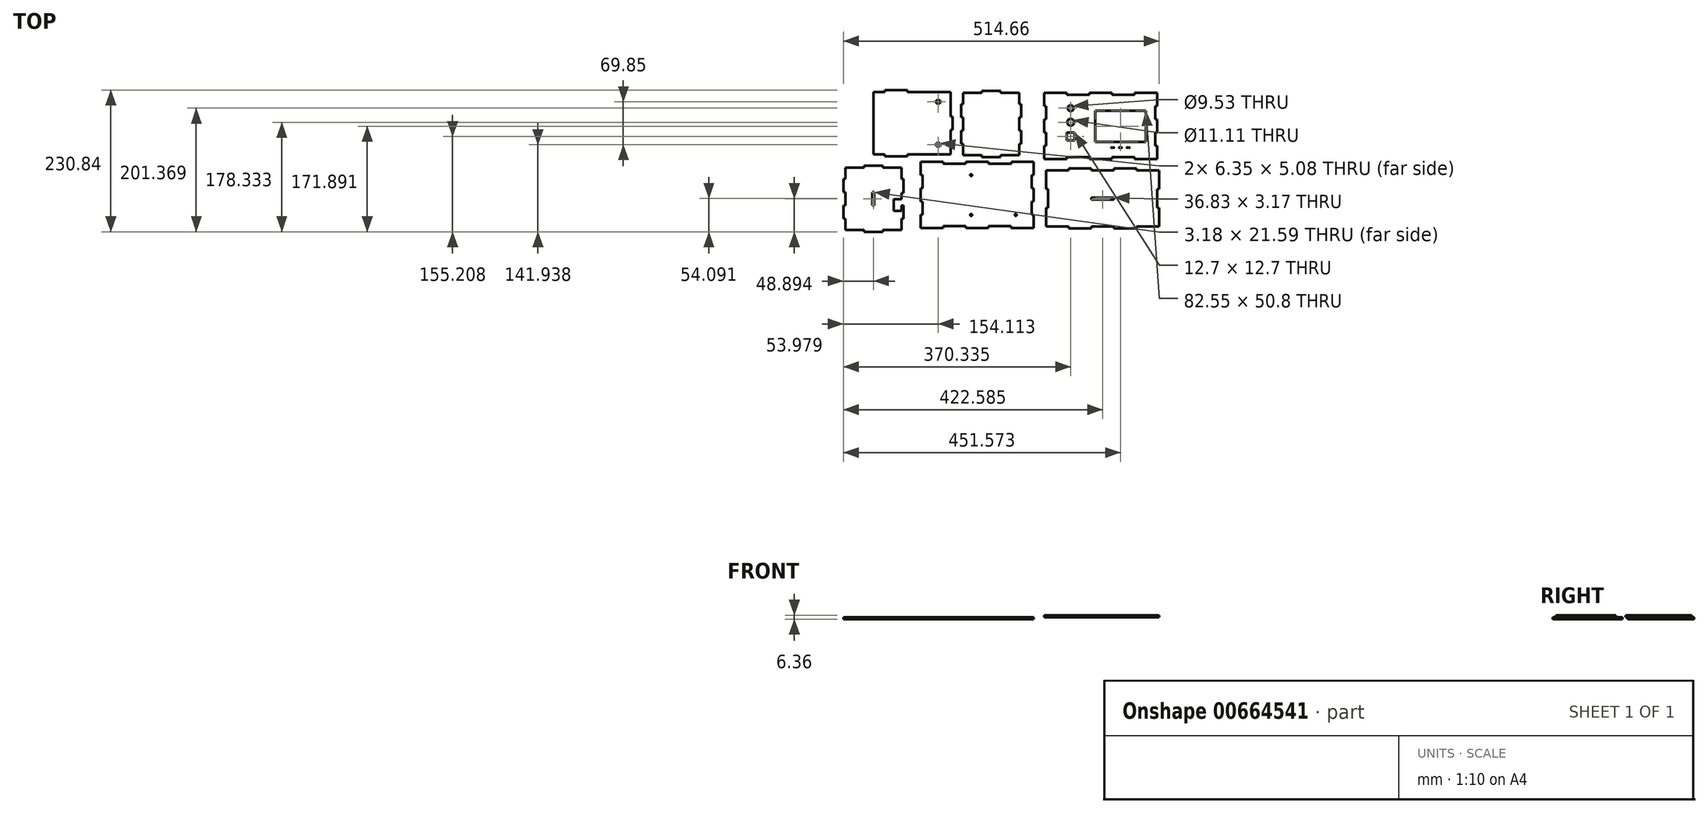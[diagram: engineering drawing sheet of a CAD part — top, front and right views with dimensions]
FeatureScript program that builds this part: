
annotation { "Feature Type Name" : "Feature", "Feature Type Description" : "" }
export const myFeature = defineFeature(function(context is Context, id is Id, definition is map)
    precondition{}
    {
        {
            var Q0;
            Q0=qCreatedBy(makeId("Top.planeOp"),FACE);
            var sketch = newSketch(context, id + "F0", { "sketchPlane" : qUnion([Q0])});
            skLineSegment(sketch, "E0", {"start": v(0, 18.41) * mm, "end": v(0, 40) * mm});
            skLineSegment(sketch, "E1", {"start": v(33.65, 101.6) * mm, "end": v(70.48, 101.6) * mm});
            skLineSegment(sketch, "E2", {"start": v(33.66, 0) * mm, "end": v(70.48, 0) * mm});
            skLineSegment(sketch, "E3", {"start": v(177.8, 18.41) * mm, "end": v(177.8, 40) * mm});
            skCircle(sketch, "E4", {"center": v(39.83, 56.57) * mm, "radius": 5.56 * mm});
            skLineSegment(sketch, "E5.bottom", {"start": v(33.48, 39.8) * mm, "end": v(46.18, 39.8) * mm});
            skLineSegment(sketch, "E5.top", {"start": v(33.48, 27.1) * mm, "end": v(46.18, 27.1) * mm});
            skLineSegment(sketch, "E5.left", {"start": v(33.48, 39.8) * mm, "end": v(33.48, 27.1) * mm});
            skLineSegment(sketch, "E5.right", {"start": v(46.18, 39.8) * mm, "end": v(46.18, 27.1) * mm});
            skPoint(sketch, "E5.middle", {"position": v(39.83, 33.45) * mm});
            skPoint(sketch, "E6.orphan", {"position": v(39.83, 51.02) * mm});
            skPoint(sketch, "E7.trimOffspring.end.orphan", {"position": v(39.83, 15.88) * mm});
            skLineSegment(sketch, "E8", {"start": v(39.83, 56.57) * mm, "end": v(39.83, 62.13) * mm});
            skCircle(sketch, "E9", {"center": v(39.83, 79.6) * mm, "radius": 4.76 * mm});
            skLineSegment(sketch, "E10.bottom", {"start": v(79.79, 75.53) * mm, "end": v(162.34, 75.53) * mm});
            skLineSegment(sketch, "E10.top", {"start": v(79.79, 24.73) * mm, "end": v(162.34, 24.73) * mm});
            skLineSegment(sketch, "E10.left", {"start": v(79.79, 75.53) * mm, "end": v(79.79, 24.73) * mm});
            skLineSegment(sketch, "E10.right", {"start": v(162.34, 75.53) * mm, "end": v(162.34, 24.73) * mm});
            skPoint(sketch, "E10.middle", {"position": v(121.06, 50.13) * mm});
            skPoint(sketch, "E10.middle.positionSnap0", {"position": v(174.63, 50.13) * mm});
            skPoint(sketch, "E10.centerSnap0", {"position": v(174.63, 50.13) * mm});
            skLineSegment(sketch, "E11", {"start": v(122.02, 15.42) * mm, "end": v(122.65, 15.42) * mm});
            skLineSegment(sketch, "E12", {"start": v(122.65, 15.42) * mm, "end": v(123.29, 15.42) * mm});
            skLineSegment(sketch, "E13", {"start": v(132.18, 15.42) * mm, "end": v(132.81, 15.42) * mm});
            skLineSegment(sketch, "E14.MirrorCS", {"start": v(120.11, 15.42) * mm, "end": v(119.48, 15.42) * mm});
            skLineSegment(sketch, "E15.MirrorCS", {"start": v(119.48, 15.42) * mm, "end": v(118.84, 15.42) * mm});
            skLineSegment(sketch, "E16.MirrorCS", {"start": v(109.95, 15.42) * mm, "end": v(109.32, 15.42) * mm});
            skCircle(sketch, "E17", {"center": v(119.48, 15.42) * mm, "radius": 0.64 * mm});
            skCircle(sketch, "E18", {"center": v(122.65, 15.42) * mm, "radius": 0.64 * mm});
            skCircle(sketch, "E19", {"center": v(132.18, 15.42) * mm, "radius": 0.64 * mm});
            skCircle(sketch, "E20", {"center": v(135.35, 15.42) * mm, "radius": 0.64 * mm});
            skCircle(sketch, "E21", {"center": v(109.95, 15.42) * mm, "radius": 0.64 * mm});
            skCircle(sketch, "E22", {"center": v(106.78, 15.42) * mm, "radius": 0.64 * mm});
            skLineSegment(sketch, "E23.trimOffspring", {"start": v(110.59, 15.42) * mm, "end": v(109.95, 15.42) * mm});
            skLineSegment(sketch, "E24.trimOffspring", {"start": v(131.54, 15.42) * mm, "end": v(132.18, 15.42) * mm});
            skLineSegment(sketch, "E25.trimOffspring", {"start": v(134.72, 15.42) * mm, "end": v(135.35, 15.42) * mm});
            skLineSegment(sketch, "E26.trimOffspring", {"start": v(107.41, 15.42) * mm, "end": v(106.78, 15.42) * mm});
            skLineSegment(sketch, "E27.bottom", {"start": v(33.65, 104.77) * mm, "end": v(-3.17, 104.77) * mm});
            skLineSegment(sketch, "E27.left", {"start": v(180.97, 104.78) * mm, "end": v(180.97, 83.19) * mm});
            skPoint(sketch, "E27.middle", {"position": v(88.9, 50.8) * mm});
            skPoint(sketch, "E27.middle.positionSnap0", {"position": v(177.8, 50.8) * mm});
            skPoint(sketch, "E27.middle.positionSnap1", {"position": v(88.9, 101.6) * mm});
            skPoint(sketch, "E27.centerSnap0", {"position": v(177.8, 50.8) * mm});
            skPoint(sketch, "E27.centerSnap1", {"position": v(88.9, 101.6) * mm});
            skLineSegment(sketch, "E28", {"start": v(-3.17, 104.77) * mm, "end": v(33.66, 104.77) * mm});
            skLineSegment(sketch, "E29.bottom", {"start": v(107.31, 104.77) * mm, "end": v(70.48, 104.77) * mm});
            skLineSegment(sketch, "E30.bottom", {"start": v(180.97, 104.78) * mm, "end": v(144.14, 104.78) * mm});
            skLineSegment(sketch, "E31", {"start": v(-3.17, -3.18) * mm, "end": v(33.66, -3.18) * mm});
            skLineSegment(sketch, "E32.bottom", {"start": v(107.31, -3.18) * mm, "end": v(70.48, -3.18) * mm});
            skLineSegment(sketch, "E33.bottom", {"start": v(180.97, -3.18) * mm, "end": v(144.14, -3.18) * mm});
            skLineSegment(sketch, "E34", {"start": v(33.65, 104.77) * mm, "end": v(33.65, 101.6) * mm});
            skLineSegment(sketch, "E35", {"start": v(70.48, 104.77) * mm, "end": v(70.48, 101.6) * mm});
            skLineSegment(sketch, "E36", {"start": v(107.31, 104.77) * mm, "end": v(107.31, 101.6) * mm});
            skLineSegment(sketch, "E37", {"start": v(144.14, 104.77) * mm, "end": v(144.14, 101.6) * mm});
            skLineSegment(sketch, "E38", {"start": v(33.66, -3.18) * mm, "end": v(33.66, 0) * mm});
            skLineSegment(sketch, "E39", {"start": v(70.48, -3.18) * mm, "end": v(70.48, 0) * mm});
            skLineSegment(sketch, "E40", {"start": v(107.31, -3.18) * mm, "end": v(107.31, 0) * mm});
            skLineSegment(sketch, "E41", {"start": v(144.14, -3.18) * mm, "end": v(144.14, 0) * mm});
            skPoint(sketch, "E42.orphan", {"position": v(180.97, -3.17) * mm});
            skLineSegment(sketch, "E43.left", {"start": v(180.97, 18.41) * mm, "end": v(180.97, -3.18) * mm});
            skLineSegment(sketch, "E44.left", {"start": v(180.97, 61.6) * mm, "end": v(180.97, 40) * mm});
            skLineSegment(sketch, "E45", {"start": v(180.97, 83.19) * mm, "end": v(177.8, 83.19) * mm});
            skLineSegment(sketch, "E46", {"start": v(177.8, 83.19) * mm, "end": v(177.8, 61.6) * mm});
            skLineSegment(sketch, "E47", {"start": v(177.8, 61.6) * mm, "end": v(180.97, 61.6) * mm});
            skLineSegment(sketch, "E48", {"start": v(180.97, 40) * mm, "end": v(177.8, 40) * mm});
            skLineSegment(sketch, "E49", {"start": v(180.97, 18.41) * mm, "end": v(177.8, 18.41) * mm});
            skLineSegment(sketch, "E50.MirrorCS", {"start": v(-3.17, 104.78) * mm, "end": v(-3.17, 83.19) * mm});
            skLineSegment(sketch, "E51.MirrorCS", {"start": v(-3.17, 83.19) * mm, "end": v(0, 83.19) * mm});
            skLineSegment(sketch, "E52.MirrorCS", {"start": v(0, 61.6) * mm, "end": v(-3.17, 61.6) * mm});
            skLineSegment(sketch, "E53.MirrorCS", {"start": v(-3.17, 61.6) * mm, "end": v(-3.17, 40) * mm});
            skLineSegment(sketch, "E54.MirrorCS", {"start": v(-3.17, 40) * mm, "end": v(0, 40) * mm});
            skLineSegment(sketch, "E55.MirrorCS", {"start": v(-3.17, 18.41) * mm, "end": v(0, 18.41) * mm});
            skLineSegment(sketch, "E56.MirrorCS", {"start": v(-3.17, 18.41) * mm, "end": v(-3.17, -3.18) * mm});
            skPoint(sketch, "E57.orphan", {"position": v(0, 101.6) * mm});
            skLineSegment(sketch, "E58.trimOffspring", {"start": v(107.31, 101.6) * mm, "end": v(144.14, 101.6) * mm});
            skPoint(sketch, "E59.orphan", {"position": v(177.8, 101.6) * mm});
            skLineSegment(sketch, "E60.trimOffspring", {"start": v(177.8, 61.6) * mm, "end": v(177.8, 83.19) * mm});
            skPoint(sketch, "E61.orphan", {"position": v(177.8, 0) * mm});
            skLineSegment(sketch, "E62.trimOffspring", {"start": v(107.31, 0) * mm, "end": v(144.14, 0) * mm});
            skLineSegment(sketch, "E63.trimOffspring", {"start": v(0, 61.6) * mm, "end": v(0, 83.19) * mm});
            skSolve(sketch);
        }
        {
            var Q0;
            Q0 = qSketchRegion(id + "F0", true);
            extrude(context, id + "F1", {"entities" : qUnion([Q0]), "depth" : 3.17 * mm, "offsetDistance" : 25.4 * mm});
        }
        {
            var Q0;
            Q0=qCreatedBy(makeId("Top.planeOp"),FACE);
            var sketch = newSketch(context, id + "F2", { "sketchPlane" : qUnion([Q0])});
            skLineSegment(sketch, "E64", {"start": v(36.83, -18.77) * mm, "end": v(73.66, -18.77) * mm});
            skLineSegment(sketch, "E65", {"start": v(0, -21.95) * mm, "end": v(36.83, -21.95) * mm});
            skLineSegment(sketch, "E66.bottom", {"start": v(110.49, -21.95) * mm, "end": v(73.66, -21.95) * mm});
            skLineSegment(sketch, "E67.bottom", {"start": v(184.15, -21.95) * mm, "end": v(147.32, -21.95) * mm});
            skLineSegment(sketch, "E68", {"start": v(36.83, -21.95) * mm, "end": v(36.83, -18.77) * mm});
            skLineSegment(sketch, "E69", {"start": v(73.66, -21.95) * mm, "end": v(73.66, -18.77) * mm});
            skLineSegment(sketch, "E70", {"start": v(110.49, -21.95) * mm, "end": v(110.49, -18.77) * mm});
            skLineSegment(sketch, "E71", {"start": v(147.32, -21.95) * mm, "end": v(147.32, -18.77) * mm});
            skPoint(sketch, "E72.orphan", {"position": v(184.15, -21.95) * mm});
            skLineSegment(sketch, "E73.trimOffspring", {"start": v(110.49, -18.77) * mm, "end": v(147.32, -18.77) * mm});
            skLineSegment(sketch, "E74.MirrorCS", {"start": v(184.15, -113.39) * mm, "end": v(147.32, -113.39) * mm});
            skLineSegment(sketch, "E75.MirrorCS", {"start": v(36.83, -113.39) * mm, "end": v(36.83, -116.56) * mm});
            skLineSegment(sketch, "E76.MirrorCS", {"start": v(73.66, -113.39) * mm, "end": v(73.66, -116.56) * mm});
            skLineSegment(sketch, "E77.MirrorCS", {"start": v(110.49, -113.39) * mm, "end": v(110.49, -116.56) * mm});
            skLineSegment(sketch, "E78.MirrorCS", {"start": v(147.32, -113.39) * mm, "end": v(147.32, -116.56) * mm});
            skLineSegment(sketch, "E79.MirrorCS", {"start": v(110.49, -113.39) * mm, "end": v(73.66, -113.39) * mm});
            skLineSegment(sketch, "E80.MirrorCS", {"start": v(36.83, -116.56) * mm, "end": v(73.66, -116.56) * mm});
            skLineSegment(sketch, "E81.MirrorCS", {"start": v(0, -113.39) * mm, "end": v(36.83, -113.39) * mm});
            skLineSegment(sketch, "E82.MirrorCS", {"start": v(110.49, -116.56) * mm, "end": v(147.32, -116.56) * mm});
            skPoint(sketch, "E83.start.orphan", {"position": v(184.15, -67.67) * mm});
            skLineSegment(sketch, "E84", {"start": v(0, -21.95) * mm, "end": v(0, -52.43) * mm});
            skLineSegment(sketch, "E85", {"start": v(0, -82.9) * mm, "end": v(0, -113.39) * mm});
            skLineSegment(sketch, "E86", {"start": v(0, -52.43) * mm, "end": v(3.18, -52.43) * mm});
            skLineSegment(sketch, "E87", {"start": v(3.18, -52.43) * mm, "end": v(3.18, -82.9) * mm});
            skLineSegment(sketch, "E88", {"start": v(3.18, -82.9) * mm, "end": v(0, -82.9) * mm});
            skPoint(sketch, "E89.end.orphan", {"position": v(184.15, -113.39) * mm});
            skLineSegment(sketch, "E90.MirrorCS", {"start": v(184.15, -52.43) * mm, "end": v(180.97, -52.43) * mm});
            skLineSegment(sketch, "E91.MirrorCS", {"start": v(180.97, -82.9) * mm, "end": v(184.15, -82.9) * mm});
            skLineSegment(sketch, "E92.MirrorCS", {"start": v(184.15, -21.95) * mm, "end": v(184.15, -52.43) * mm});
            skLineSegment(sketch, "E93.MirrorCS", {"start": v(180.97, -52.43) * mm, "end": v(180.97, -82.9) * mm});
            skLineSegment(sketch, "E94.MirrorCS", {"start": v(184.15, -82.9) * mm, "end": v(184.15, -113.39) * mm});
            skLineSegment(sketch, "E95", {"start": v(73.66, -67.67) * mm, "end": v(73.66, -66.08) * mm});
            skPoint(sketch, "E95.startSnap0", {"position": v(3.18, -67.67) * mm});
            skLineSegment(sketch, "E96", {"start": v(73.66, -66.08) * mm, "end": v(110.49, -66.08) * mm});
            skLineSegment(sketch, "E97.MirrorCS", {"start": v(73.66, -67.67) * mm, "end": v(73.66, -69.26) * mm});
            skLineSegment(sketch, "E98.MirrorCS", {"start": v(73.66, -69.26) * mm, "end": v(110.49, -69.26) * mm});
            skLineSegment(sketch, "E99", {"start": v(110.49, -66.08) * mm, "end": v(110.49, -69.26) * mm});
            skSolve(sketch);
        }
        {
            var Q0;
            Q0 = qSketchRegion(id + "F2", true);
            extrude(context, id + "F3", {"entities" : qUnion([Q0]), "depth" : 3.17 * mm, "offsetDistance" : 25.4 * mm});
        }
        {
            var Q0;
            Q0=qCreatedBy(makeId("Top.planeOp"),FACE);
            var sketch = newSketch(context, id + "F4", { "sketchPlane" : qUnion([Q0])});
            skLineSegment(sketch, "E100", {"start": v(-41.1, 86.36) * mm, "end": v(-41.1, 64.77) * mm});
            skLineSegment(sketch, "E101.left", {"start": v(-44.27, 3.17) * mm, "end": v(-44.27, 21.59) * mm});
            skPoint(sketch, "E102.orphan", {"position": v(-44.27, 107.95) * mm});
            skLineSegment(sketch, "E103.left", {"start": v(-44.27, 86.36) * mm, "end": v(-44.27, 104.78) * mm});
            skLineSegment(sketch, "E104.left", {"start": v(-44.27, 43.18) * mm, "end": v(-44.27, 64.77) * mm});
            skLineSegment(sketch, "E105", {"start": v(-44.27, 21.59) * mm, "end": v(-41.1, 21.59) * mm});
            skLineSegment(sketch, "E106", {"start": v(-41.1, 21.59) * mm, "end": v(-41.1, 43.18) * mm});
            skLineSegment(sketch, "E107", {"start": v(-41.1, 43.18) * mm, "end": v(-44.27, 43.18) * mm});
            skLineSegment(sketch, "E108", {"start": v(-44.27, 64.77) * mm, "end": v(-41.1, 64.77) * mm});
            skLineSegment(sketch, "E109", {"start": v(-44.27, 86.36) * mm, "end": v(-41.1, 86.36) * mm});
            skLineSegment(sketch, "E110.trimOffspring", {"start": v(-41.1, 43.18) * mm, "end": v(-41.1, 21.59) * mm});
            skLineSegment(sketch, "E111", {"start": v(-44.27, 3.17) * mm, "end": v(-74.75, 3.17) * mm});
            skLineSegment(sketch, "E112", {"start": v(-105.23, 3.17) * mm, "end": v(-135.71, 3.17) * mm});
            skLineSegment(sketch, "E113", {"start": v(-74.75, 3.17) * mm, "end": v(-74.75, 0) * mm});
            skLineSegment(sketch, "E114", {"start": v(-74.75, 0) * mm, "end": v(-105.23, 0) * mm});
            skLineSegment(sketch, "E115", {"start": v(-105.23, 0) * mm, "end": v(-105.23, 3.17) * mm});
            skPoint(sketch, "E116.startSnap0", {"position": v(-44.27, 53.97) * mm});
            skLineSegment(sketch, "E117.MirrorCS", {"start": v(-105.23, 107.95) * mm, "end": v(-105.23, 104.78) * mm});
            skLineSegment(sketch, "E118.MirrorCS", {"start": v(-74.75, 104.78) * mm, "end": v(-74.75, 107.95) * mm});
            skLineSegment(sketch, "E119.MirrorCS", {"start": v(-105.23, 104.78) * mm, "end": v(-135.71, 104.78) * mm});
            skLineSegment(sketch, "E120.MirrorCS", {"start": v(-44.27, 104.78) * mm, "end": v(-74.75, 104.78) * mm});
            skLineSegment(sketch, "E121.MirrorCS", {"start": v(-74.75, 107.95) * mm, "end": v(-105.23, 107.95) * mm});
            skPoint(sketch, "E116.start.orphan", {"position": v(-62.22, 53.97) * mm});
            skLineSegment(sketch, "E122", {"start": v(-90, 89.85) * mm, "end": v(-90, 62.74) * mm});
            skPoint(sketch, "E122.startSnap0", {"position": v(-90, 107.95) * mm});
            skLineSegment(sketch, "E123.MirrorCS", {"start": v(-135.71, 21.59) * mm, "end": v(-138.89, 21.59) * mm});
            skLineSegment(sketch, "E124.MirrorCS", {"start": v(-135.71, 64.77) * mm, "end": v(-138.89, 64.77) * mm});
            skLineSegment(sketch, "E125.MirrorCS", {"start": v(-135.71, 86.36) * mm, "end": v(-138.89, 86.36) * mm});
            skLineSegment(sketch, "E126.MirrorCS", {"start": v(-138.89, 43.18) * mm, "end": v(-135.71, 43.18) * mm});
            skLineSegment(sketch, "E127.MirrorCS", {"start": v(-138.89, 21.59) * mm, "end": v(-138.89, 43.18) * mm});
            skLineSegment(sketch, "E128.MirrorCS", {"start": v(-135.71, 3.17) * mm, "end": v(-135.71, 21.59) * mm});
            skPoint(sketch, "E129.MirrorP", {"position": v(-135.71, 53.97) * mm});
            skLineSegment(sketch, "E130.MirrorCS", {"start": v(-135.71, 3.17) * mm, "end": v(-105.23, 3.17) * mm});
            skLineSegment(sketch, "E131.MirrorCS", {"start": v(-135.71, 43.18) * mm, "end": v(-135.71, 64.77) * mm});
            skLineSegment(sketch, "E132.MirrorCS", {"start": v(-135.71, 86.36) * mm, "end": v(-135.71, 104.78) * mm});
            skLineSegment(sketch, "E133.MirrorCS", {"start": v(-138.89, 43.18) * mm, "end": v(-138.89, 21.59) * mm});
            skLineSegment(sketch, "E134.MirrorCS", {"start": v(-138.89, 86.36) * mm, "end": v(-138.89, 64.77) * mm});
            skSolve(sketch);
        }
        {
            var Q0;
            Q0 = qSketchRegion(id + "F4", true);
            extrude(context, id + "F5", {"entities" : qUnion([Q0]), "oppositeDirection" : true, "depth" : 3.17 * mm, "offsetDistance" : 25.4 * mm});
        }
        {
            var Q0;
            Q0=qCreatedBy(makeId("Top.planeOp"),FACE);
            var sketch = newSketch(context, id + "F6", { "sketchPlane" : qUnion([Q0])});
            skLineSegment(sketch, "E135", {"start": v(-201.23, -94.42) * mm, "end": v(-201.23, -72.83) * mm});
            skLineSegment(sketch, "E136", {"start": v(-167.58, -11.23) * mm, "end": v(-130.75, -11.23) * mm});
            skLineSegment(sketch, "E137", {"start": v(-167.58, -112.83) * mm, "end": v(-130.75, -112.83) * mm});
            skLineSegment(sketch, "E138", {"start": v(-23.43, -94.42) * mm, "end": v(-23.43, -72.83) * mm});
            skLineSegment(sketch, "E139.bottom", {"start": v(-167.58, -8.06) * mm, "end": v(-204.4, -8.06) * mm});
            skLineSegment(sketch, "E139.left", {"start": v(-20.26, -8.06) * mm, "end": v(-20.26, -29.65) * mm});
            skPoint(sketch, "E139.middle.positionSnap0", {"position": v(-23.43, -62.03) * mm});
            skPoint(sketch, "E139.middle.positionSnap1", {"position": v(-112.33, -11.23) * mm});
            skPoint(sketch, "E139.centerSnap0", {"position": v(-23.43, -62.03) * mm});
            skPoint(sketch, "E139.centerSnap1", {"position": v(-112.33, -11.23) * mm});
            skLineSegment(sketch, "E140", {"start": v(-204.4, -8.06) * mm, "end": v(-167.58, -8.06) * mm});
            skLineSegment(sketch, "E141.bottom", {"start": v(-93.92, -8.06) * mm, "end": v(-130.75, -8.06) * mm});
            skLineSegment(sketch, "E142.bottom", {"start": v(-20.26, -8.06) * mm, "end": v(-56.46, -8.06) * mm});
            skLineSegment(sketch, "E143", {"start": v(-204.4, -116) * mm, "end": v(-167.58, -116) * mm});
            skLineSegment(sketch, "E144.bottom", {"start": v(-93.92, -116) * mm, "end": v(-130.75, -116) * mm});
            skLineSegment(sketch, "E145.bottom", {"start": v(-20.26, -116) * mm, "end": v(-57.09, -116) * mm});
            skLineSegment(sketch, "E146", {"start": v(-167.58, -8.06) * mm, "end": v(-167.58, -11.23) * mm});
            skLineSegment(sketch, "E147", {"start": v(-130.75, -8.06) * mm, "end": v(-130.75, -11.23) * mm});
            skLineSegment(sketch, "E148", {"start": v(-93.92, -8.06) * mm, "end": v(-93.92, -11.23) * mm});
            skLineSegment(sketch, "E149", {"start": v(-56.46, -8.06) * mm, "end": v(-56.46, -11.23) * mm});
            skLineSegment(sketch, "E150", {"start": v(-167.58, -116) * mm, "end": v(-167.58, -112.83) * mm});
            skLineSegment(sketch, "E151", {"start": v(-130.75, -116) * mm, "end": v(-130.75, -112.83) * mm});
            skLineSegment(sketch, "E152", {"start": v(-93.92, -116) * mm, "end": v(-93.92, -112.83) * mm});
            skLineSegment(sketch, "E153", {"start": v(-57.09, -116) * mm, "end": v(-57.09, -112.83) * mm});
            skPoint(sketch, "E154.orphan", {"position": v(-20.26, -116) * mm});
            skLineSegment(sketch, "E155.left", {"start": v(-20.26, -94.42) * mm, "end": v(-20.26, -116) * mm});
            skLineSegment(sketch, "E156.left", {"start": v(-20.26, -51.24) * mm, "end": v(-20.26, -72.83) * mm});
            skLineSegment(sketch, "E157", {"start": v(-20.26, -29.65) * mm, "end": v(-23.43, -29.65) * mm});
            skLineSegment(sketch, "E158", {"start": v(-23.43, -29.65) * mm, "end": v(-23.43, -51.24) * mm});
            skLineSegment(sketch, "E159", {"start": v(-23.43, -51.24) * mm, "end": v(-20.26, -51.24) * mm});
            skLineSegment(sketch, "E160", {"start": v(-20.26, -72.83) * mm, "end": v(-23.43, -72.83) * mm});
            skLineSegment(sketch, "E161", {"start": v(-20.26, -94.42) * mm, "end": v(-23.43, -94.42) * mm});
            skLineSegment(sketch, "E162.MirrorCS", {"start": v(-204.4, -8.06) * mm, "end": v(-204.4, -29.65) * mm});
            skLineSegment(sketch, "E163.MirrorCS", {"start": v(-204.4, -29.65) * mm, "end": v(-201.23, -29.65) * mm});
            skLineSegment(sketch, "E164.MirrorCS", {"start": v(-201.23, -51.24) * mm, "end": v(-204.4, -51.24) * mm});
            skLineSegment(sketch, "E165.MirrorCS", {"start": v(-204.4, -51.24) * mm, "end": v(-204.4, -72.83) * mm});
            skLineSegment(sketch, "E166.MirrorCS", {"start": v(-204.4, -72.83) * mm, "end": v(-201.23, -72.83) * mm});
            skLineSegment(sketch, "E167.MirrorCS", {"start": v(-204.4, -94.42) * mm, "end": v(-201.23, -94.42) * mm});
            skLineSegment(sketch, "E168.MirrorCS", {"start": v(-204.4, -94.42) * mm, "end": v(-204.4, -116) * mm});
            skPoint(sketch, "E169.orphan", {"position": v(-201.23, -11.23) * mm});
            skLineSegment(sketch, "E170.trimOffspring", {"start": v(-93.92, -11.23) * mm, "end": v(-56.46, -11.23) * mm});
            skPoint(sketch, "E171.orphan", {"position": v(-23.43, -11.23) * mm});
            skLineSegment(sketch, "E172.trimOffspring", {"start": v(-23.43, -51.24) * mm, "end": v(-23.43, -29.65) * mm});
            skPoint(sketch, "E173.orphan", {"position": v(-23.43, -112.83) * mm});
            skLineSegment(sketch, "E174.trimOffspring", {"start": v(-93.92, -112.83) * mm, "end": v(-57.09, -112.83) * mm});
            skLineSegment(sketch, "E175.trimOffspring", {"start": v(-201.23, -51.24) * mm, "end": v(-201.23, -29.65) * mm});
            skCircle(sketch, "E176.MirrorC", {"center": v(-122.28, -94.42) * mm, "radius": 1.59 * mm});
            skCircle(sketch, "E177.MirrorC", {"center": v(-122.28, -29.42) * mm, "radius": 1.59 * mm});
            skPoint(sketch, "E178.MirrorP", {"position": v(-127.48, -94.42) * mm});
            skPoint(sketch, "E179.MirrorP", {"position": v(-127.48, -29.42) * mm});
            skCircle(sketch, "E180", {"center": v(-49.67, -94.3) * mm, "radius": 1.59 * mm});
            skSolve(sketch);
        }
        {
            var Q0;
            Q0 = qSketchRegion(id + "F6", true);
            extrude(context, id + "F7", {"entities" : qUnion([Q0]), "oppositeDirection" : true, "depth" : 3.17 * mm, "offsetDistance" : 25.4 * mm});
        }
        {
            var Q0;
            Q0=qCreatedBy(makeId("Top.planeOp"),FACE);
            var sketch = newSketch(context, id + "F8", { "sketchPlane" : qUnion([Q0])});
            skLineSegment(sketch, "E181", {"start": v(-281.25, 105.9) * mm, "end": v(-262.84, 105.9) * mm});
            skLineSegment(sketch, "E182", {"start": v(-281.25, 4.3) * mm, "end": v(-262.84, 4.3) * mm});
            skLineSegment(sketch, "E183", {"start": v(-155.52, 22.72) * mm, "end": v(-155.52, 44.3) * mm});
            skPoint(sketch, "E184.centerSnap1", {"position": v(-244.42, 105.9) * mm});
            skLineSegment(sketch, "E185.bottom", {"start": v(-226, 109.08) * mm, "end": v(-262.84, 109.08) * mm});
            skLineSegment(sketch, "E186.bottom", {"start": v(-226, 1.13) * mm, "end": v(-262.84, 1.13) * mm});
            skLineSegment(sketch, "E187", {"start": v(-262.84, 109.08) * mm, "end": v(-262.84, 105.9) * mm});
            skLineSegment(sketch, "E188", {"start": v(-226, 109.08) * mm, "end": v(-226, 105.9) * mm});
            skLineSegment(sketch, "E189", {"start": v(-262.84, 1.13) * mm, "end": v(-262.84, 4.3) * mm});
            skLineSegment(sketch, "E190", {"start": v(-226, 1.13) * mm, "end": v(-226, 4.3) * mm});
            skLineSegment(sketch, "E191.left", {"start": v(-152.35, 65.9) * mm, "end": v(-152.35, 44.3) * mm});
            skLineSegment(sketch, "E192", {"start": v(-155.52, 87.49) * mm, "end": v(-155.52, 65.9) * mm});
            skLineSegment(sketch, "E193", {"start": v(-155.52, 65.9) * mm, "end": v(-152.35, 65.9) * mm});
            skLineSegment(sketch, "E194", {"start": v(-152.35, 44.3) * mm, "end": v(-155.52, 44.3) * mm});
            skLineSegment(sketch, "E195.trimOffspring", {"start": v(-226, 105.9) * mm, "end": v(-189.18, 105.9) * mm});
            skPoint(sketch, "E196.orphan", {"position": v(-155.52, 105.9) * mm});
            skLineSegment(sketch, "E197.trimOffspring", {"start": v(-155.52, 65.9) * mm, "end": v(-155.52, 87.49) * mm});
            skPoint(sketch, "E198.orphan", {"position": v(-155.52, 4.3) * mm});
            skLineSegment(sketch, "E199.trimOffspring", {"start": v(-226, 4.3) * mm, "end": v(-189.18, 4.3) * mm});
            skLineSegment(sketch, "E200", {"start": v(-189.18, 105.9) * mm, "end": v(-155.52, 105.9) * mm});
            skLineSegment(sketch, "E201", {"start": v(-155.52, 87.49) * mm, "end": v(-155.52, 105.9) * mm});
            skLineSegment(sketch, "E202", {"start": v(-155.52, 22.72) * mm, "end": v(-155.52, 4.3) * mm});
            skLineSegment(sketch, "E203", {"start": v(-189.18, 4.3) * mm, "end": v(-155.52, 4.3) * mm});
            skLineSegment(sketch, "E204", {"start": v(-281.25, 105.9) * mm, "end": v(-281.25, 4.3) * mm});
            skPoint(sketch, "E205.startSnap0", {"position": v(-152.35, 55.1) * mm});
            skLineSegment(sketch, "E206.bottom", {"start": v(-173.22, 87.49) * mm, "end": v(-179.57, 87.49) * mm});
            skLineSegment(sketch, "E206.top", {"start": v(-173.22, 92.57) * mm, "end": v(-179.57, 92.57) * mm});
            skLineSegment(sketch, "E206.left", {"start": v(-173.22, 87.49) * mm, "end": v(-173.22, 92.57) * mm});
            skLineSegment(sketch, "E206.right", {"start": v(-179.57, 87.49) * mm, "end": v(-179.57, 92.57) * mm});
            skLineSegment(sketch, "E207.MirrorCS", {"start": v(-173.22, 22.72) * mm, "end": v(-179.57, 22.72) * mm});
            skLineSegment(sketch, "E208.MirrorCS", {"start": v(-173.22, 22.72) * mm, "end": v(-173.22, 17.64) * mm});
            skLineSegment(sketch, "E209.MirrorCS", {"start": v(-179.57, 22.72) * mm, "end": v(-179.57, 17.64) * mm});
            skLineSegment(sketch, "E210.MirrorCS", {"start": v(-173.22, 17.64) * mm, "end": v(-179.57, 17.64) * mm});
            skSolve(sketch);
        }
        {
            var Q0;
            Q0 = qSketchRegion(id + "F8", true);
            extrude(context, id + "F9", {"entities" : qUnion([Q0]), "oppositeDirection" : true, "depth" : 3.17 * mm, "offsetDistance" : 25.4 * mm});
        }
        {
            var Q0;
            Q0=qCreatedBy(makeId("Top.planeOp"),FACE);
            var sketch = newSketch(context, id + "F10", { "sketchPlane" : qUnion([Q0])});
            skLineSegment(sketch, "E211", {"start": v(-232.72, -35.4) * mm, "end": v(-232.72, -58.44) * mm});
            skLineSegment(sketch, "E212.left", {"start": v(-235.9, -118.58) * mm, "end": v(-235.9, -100.17) * mm});
            skPoint(sketch, "E213.orphan", {"position": v(-235.9, -13.8) * mm});
            skLineSegment(sketch, "E214.left", {"start": v(-235.9, -35.4) * mm, "end": v(-235.9, -16.98) * mm});
            skLineSegment(sketch, "E215.left", {"start": v(-236, -68.5) * mm, "end": v(-236, -58.44) * mm});
            skLineSegment(sketch, "E216", {"start": v(-235.9, -100.17) * mm, "end": v(-232.72, -100.17) * mm});
            skLineSegment(sketch, "E217", {"start": v(-232.72, -100.17) * mm, "end": v(-232.72, -78.58) * mm});
            skLineSegment(sketch, "E218", {"start": v(-232.72, -78.58) * mm, "end": v(-236, -78.58) * mm});
            skLineSegment(sketch, "E219", {"start": v(-236, -58.44) * mm, "end": v(-232.72, -58.44) * mm});
            skLineSegment(sketch, "E220", {"start": v(-235.9, -35.4) * mm, "end": v(-232.72, -35.4) * mm});
            skLineSegment(sketch, "E221.trimOffspring", {"start": v(-232.72, -78.58) * mm, "end": v(-232.72, -100.17) * mm});
            skLineSegment(sketch, "E222", {"start": v(-235.9, -118.58) * mm, "end": v(-266.38, -118.58) * mm});
            skLineSegment(sketch, "E223", {"start": v(-296.86, -118.58) * mm, "end": v(-327.34, -118.58) * mm});
            skLineSegment(sketch, "E224", {"start": v(-266.38, -118.58) * mm, "end": v(-266.38, -121.76) * mm});
            skLineSegment(sketch, "E225", {"start": v(-266.38, -121.76) * mm, "end": v(-296.86, -121.76) * mm});
            skLineSegment(sketch, "E226", {"start": v(-296.86, -121.76) * mm, "end": v(-296.86, -118.58) * mm});
            skPoint(sketch, "E227.startSnap0", {"position": v(-236, -68.5) * mm});
            skLineSegment(sketch, "E228.MirrorCS", {"start": v(-296.86, -13.8) * mm, "end": v(-296.86, -16.98) * mm});
            skLineSegment(sketch, "E229.MirrorCS", {"start": v(-266.38, -16.98) * mm, "end": v(-266.38, -13.8) * mm});
            skLineSegment(sketch, "E230.MirrorCS", {"start": v(-296.86, -16.98) * mm, "end": v(-327.34, -16.98) * mm});
            skLineSegment(sketch, "E231.MirrorCS", {"start": v(-235.9, -16.98) * mm, "end": v(-266.38, -16.98) * mm});
            skLineSegment(sketch, "E232.MirrorCS", {"start": v(-266.38, -13.8) * mm, "end": v(-296.86, -13.8) * mm});
            skPoint(sketch, "E233.startSnap0", {"position": v(-281.62, -13.8) * mm});
            skLineSegment(sketch, "E234.MirrorCS", {"start": v(-327.34, -100.17) * mm, "end": v(-330.51, -100.17) * mm});
            skLineSegment(sketch, "E235.MirrorCS", {"start": v(-327.34, -56.99) * mm, "end": v(-330.51, -56.99) * mm});
            skLineSegment(sketch, "E236.MirrorCS", {"start": v(-327.34, -35.4) * mm, "end": v(-330.51, -35.4) * mm});
            skLineSegment(sketch, "E237.MirrorCS", {"start": v(-330.51, -78.58) * mm, "end": v(-327.34, -78.58) * mm});
            skLineSegment(sketch, "E238.MirrorCS", {"start": v(-330.51, -100.17) * mm, "end": v(-330.51, -78.58) * mm});
            skLineSegment(sketch, "E239.MirrorCS", {"start": v(-327.34, -118.58) * mm, "end": v(-327.34, -100.17) * mm});
            skPoint(sketch, "E240.MirrorP", {"position": v(-327.34, -67.78) * mm});
            skLineSegment(sketch, "E241.MirrorCS", {"start": v(-327.34, -118.58) * mm, "end": v(-296.86, -118.58) * mm});
            skLineSegment(sketch, "E242.MirrorCS", {"start": v(-327.34, -78.58) * mm, "end": v(-327.34, -56.99) * mm});
            skLineSegment(sketch, "E243.MirrorCS", {"start": v(-327.34, -35.4) * mm, "end": v(-327.34, -16.98) * mm});
            skLineSegment(sketch, "E244.MirrorCS", {"start": v(-330.51, -78.58) * mm, "end": v(-330.51, -100.17) * mm});
            skLineSegment(sketch, "E245.MirrorCS", {"start": v(-330.51, -35.4) * mm, "end": v(-330.51, -56.99) * mm});
            skLineSegment(sketch, "E246", {"start": v(-280.03, -56.99) * mm, "end": v(-280.03, -78.58) * mm});
            skLineSegment(sketch, "E247.MirrorCS", {"start": v(-283.2, -56.99) * mm, "end": v(-283.2, -78.58) * mm});
            skLineSegment(sketch, "E248", {"start": v(-283.2, -56.99) * mm, "end": v(-280.03, -56.99) * mm});
            skLineSegment(sketch, "E249", {"start": v(-283.2, -78.58) * mm, "end": v(-280.03, -78.58) * mm});
            skLineSegment(sketch, "E250", {"start": v(-246.58, -68.5) * mm, "end": v(-236, -68.5) * mm});
            skLineSegment(sketch, "E251", {"start": v(-236, -78.58) * mm, "end": v(-236, -81.75) * mm});
            skLineSegment(sketch, "E252", {"start": v(-236, -87.56) * mm, "end": v(-236, -81.75) * mm});
            skLineSegment(sketch, "E253", {"start": v(-236, -87.56) * mm, "end": v(-248.7, -87.56) * mm});
            skLineSegment(sketch, "E254", {"start": v(-248.7, -87.56) * mm, "end": v(-248.7, -68.5) * mm});
            skLineSegment(sketch, "E255", {"start": v(-248.7, -68.5) * mm, "end": v(-246.58, -68.5) * mm});
            skSolve(sketch);
        }
        {
            var Q0;
            Q0=makeQuery(id+"F10.imprint","IMPRINT",FACE,{"disambiguationData":[TD([[makeQuery(id+"F10.imprint","IMPRINT",EDGE,{"derivedFrom":sQuery(id+"F10.wireOp",EDGE,"E211")}),-1.0]])]});
            extrude(context, id + "F11", {"entities" : qUnion([Q0]), "oppositeDirection" : true, "depth" : 3.17 * mm, "offsetDistance" : 25.4 * mm});
        }
    });
